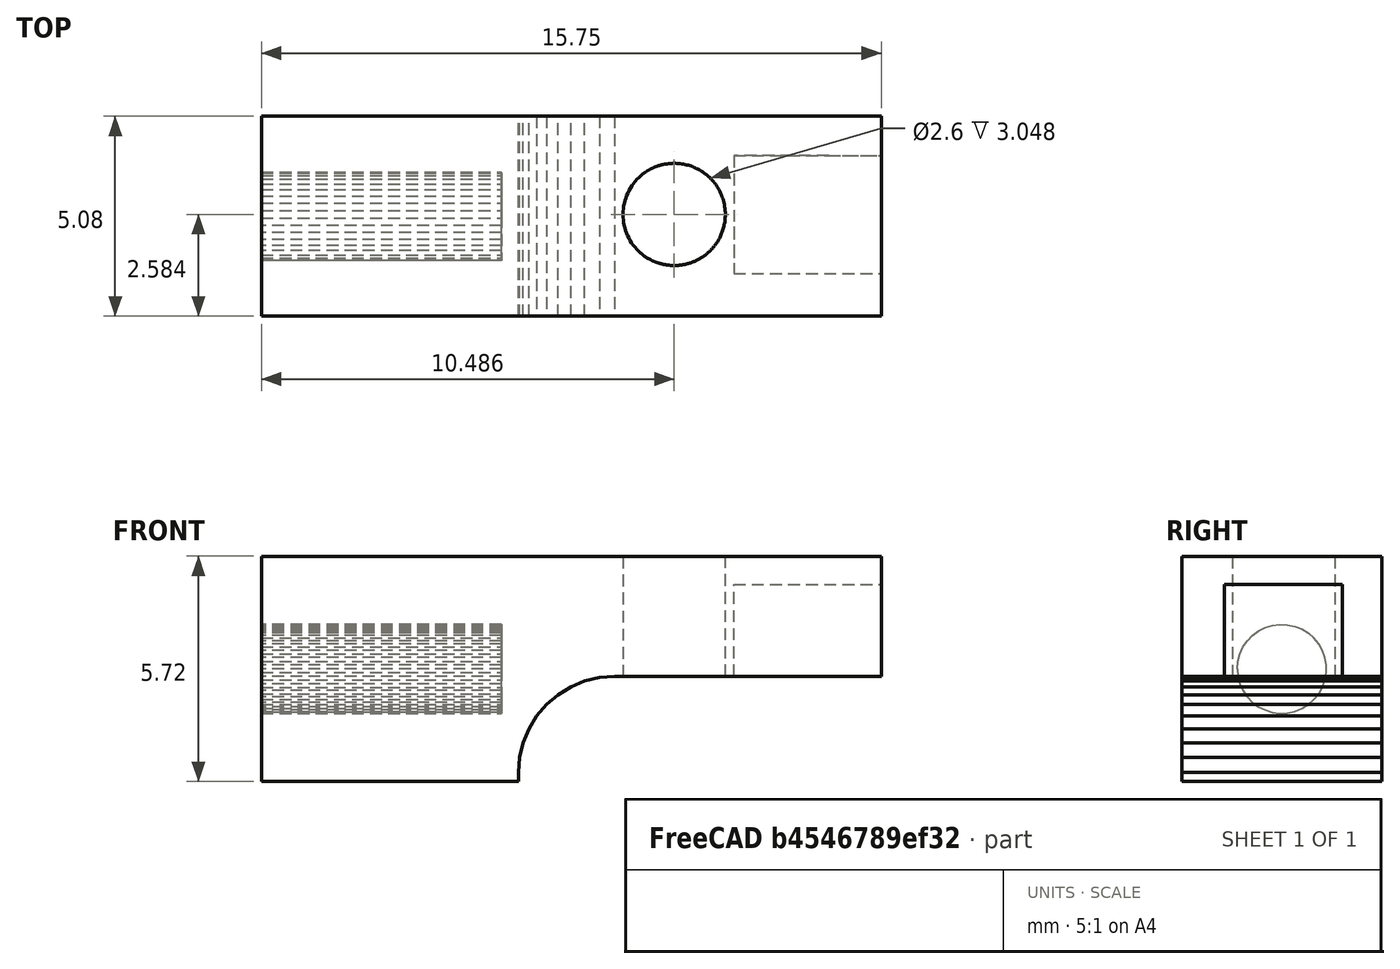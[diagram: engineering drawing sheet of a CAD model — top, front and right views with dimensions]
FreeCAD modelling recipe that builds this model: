
FCSTD DOCUMENT  (FreeCAD 0.21R33771 (Git))
Label: holder-hole
License: All rights reserved
LicenseURL: https://en.wikipedia.org/wiki/All_rights_reserved
objects: Part::Feature×1, PartDesign::FeatureBase×1, Sketcher::SketchObject×1, PartDesign::Pocket×1, PartDesign::Body×1
note: 6 computed .brp shape members not serialized (recipe doc carries the construction recipe); baked Part::Feature solids carry a one-line shape summary decoded from their .brp

FEATURE [Part::Feature] holder_Body002_solid  label="holder_Body002 (Solid)"
  shape: bbox 15.75 x 5.08 x 5.715 mm, 322 faces (baked)
FEATURE [PartDesign::FeatureBase] BaseFeature
  BaseFeature = -> holder_Body002_solid
FEATURE [Sketcher::SketchObject] Sketch
  FullyConstrained = false
  MapMode = 5
  Placement = pos=(0,0,3.667) rot=(1,0,0;3.14159rad)
  Support = -> [BaseFeature]
  sketch-geometry (1):
    g0: Circle CenterX=22.4862 CenterY=-2.5038 CenterZ=0 NormalX=0 NormalY=0 NormalZ=1 AngleXU=0 Radius=1.29896
FEATURE [PartDesign::Pocket] Pocket
  BaseFeature = -> BaseFeature
  Direction = (0,0,1)
  Length = 5
  Length2 = 5
  Profile = -> Sketch
  ReferenceAxis = -> Sketch [N_Axis]
  Type = 0
FEATURE [PartDesign::Body] Body
  BaseFeature = -> holder_Body002_solid
  Group = -> [BaseFeature,Sketch,Pocket]
  Origin = -> Origin
  Tip = -> Pocket
